# Revit family: VP153UB
name_source: partatom
category: Generic Models
revit_build: Autodesk Revit MEP 2013 (Build: 20130531_2115(x64)
units: mm (PartAtom-declared; Revit-internal decimal feet)

## types (1)
- Zip Varipoint II_ model_VP153UB
    BMS Links = No
    Base Unit Finish = White impact resistant plastic
    Button Interface = No
    Cable Length and size (If Fitted) = 1.2M
    Capacity = 15.0 L
    Control Thermostat Range = 50°C, 65°C,  80°C
    Enclosure Rating = IP24
    External Material = The casing is constructed of impact resistant plastic
    Gross Weight (When Full) = 22.5kg
    Heat Up Time = 29mins
    Insulation Material = Heat losses are minimised by the high efficiency CFC free polyurethane foam insulation.
the high efficiency CFC free polyurethane foam insulation.
    Internal Filter (if fitted) = No
    Mains Pressure Limiting Valve = offered as accessory
    Mains Water Connection = 1/2" BSP
    Mains Water Pressure _ Maximum = 0.55 Mpa
    Manufacturer = Zip Industries(UK) Ltd
    Max. Stored Water Temperature = 80°C
    Model = VP153UB
    Net Weight = 7.5kg
    Overall Height = 440
    Overall Length/Depth/Circumference = 300
    Overall Width = 300
    Power Rating = 2.2kW
    Power Supply (Voltage) = 230 (V~)
    Product Range = Wall Mounted
    Programmable Function Parameters = No
    Programmable Safety Features = No
    Shape = Rectangular
    Standby Power Loss (idle mode) = Not Known
    Supply Phase = 1
    Tank Construction Material = The inner vessel is constructed from heavy guage copper tested to 1.6MPa (16 bar),
maximum working pressure 0.55 MPa (5.5 bar).
    Type = Direct unvented water heater
    Type Comments = Direct unvented water heater
    URL = www.zipindustries.co.uk
    Unit Access Clearance Bottom = 400mm
    Unit Access Clearance Top = 250mm
    WRAS Approved = Yes
    Warranty ID = Zip Heaters (UK) Ltd warrants that, should any part fail within 12 calendar months of installation
    Wireless (WIFI) = No

## geometry (parser evidence)
native form markers: Sweep x1
no freeform markers — native parametric forms only
